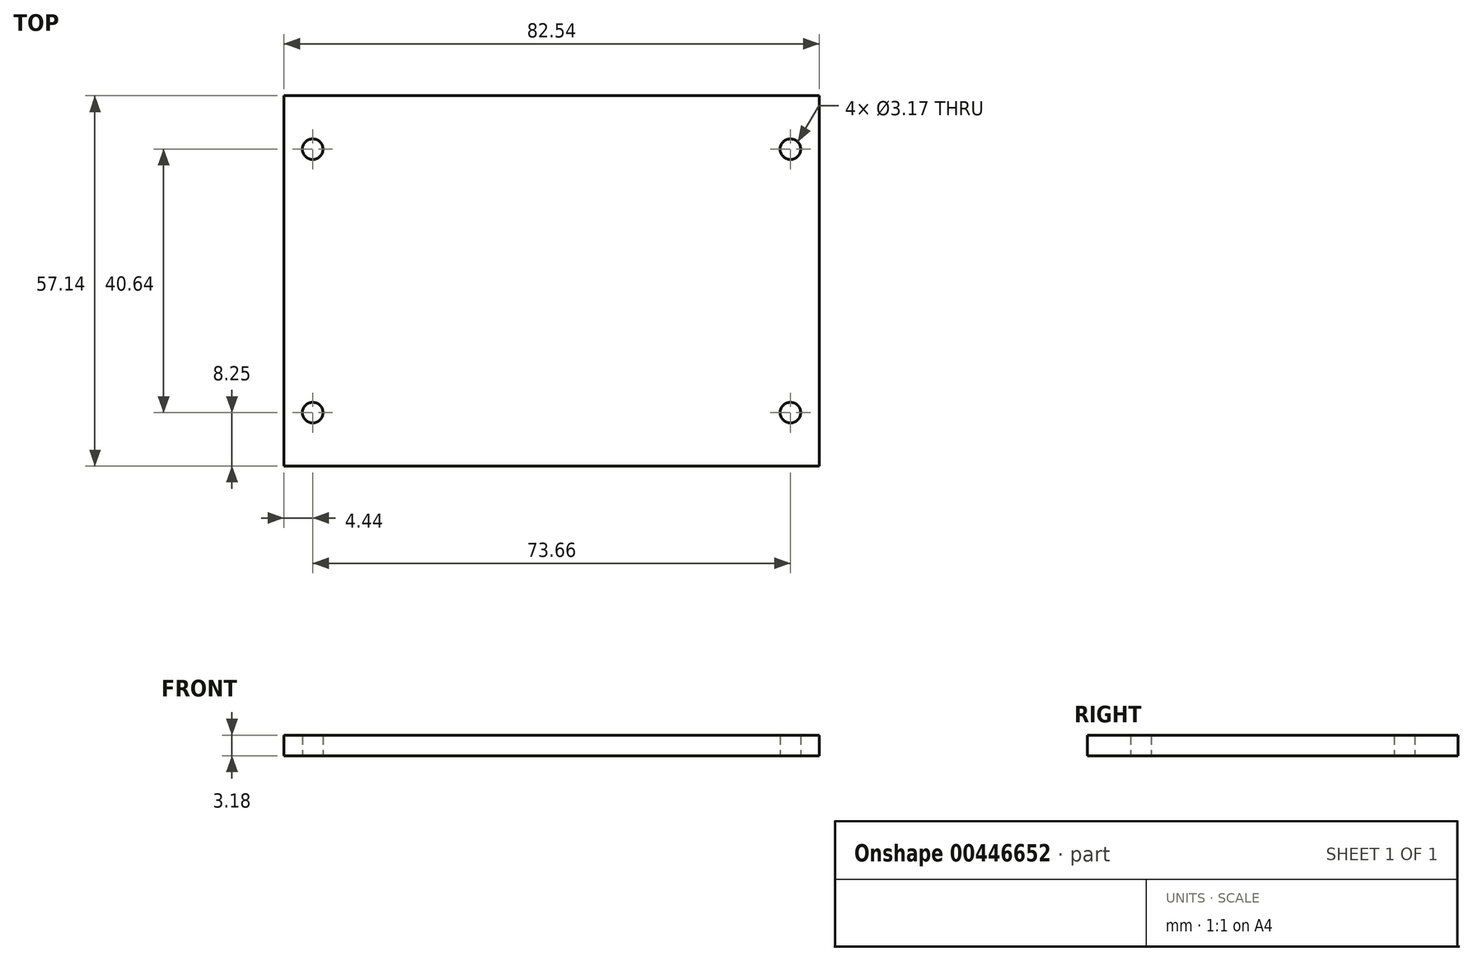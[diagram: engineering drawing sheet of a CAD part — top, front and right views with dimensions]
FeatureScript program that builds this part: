
annotation { "Feature Type Name" : "Feature", "Feature Type Description" : "" }
export const myFeature = defineFeature(function(context is Context, id is Id, definition is map)
    precondition{}
    {
        {
            var Q0;
            Q0=qCreatedBy(makeId("Top.planeOp"),FACE);
            var sketch = newSketch(context, id + "F0", { "sketchPlane" : qUnion([Q0])});
            skLineSegment(sketch, "E0.bottom", {"start": v(36.83, -20.32) * mm, "end": v(-36.83, -20.32) * mm});
            skLineSegment(sketch, "E0.top", {"start": v(36.83, 20.32) * mm, "end": v(-36.83, 20.32) * mm});
            skLineSegment(sketch, "E0.left", {"start": v(36.83, -20.32) * mm, "end": v(36.83, 20.32) * mm});
            skLineSegment(sketch, "E0.right", {"start": v(-36.83, -20.32) * mm, "end": v(-36.83, 20.32) * mm});
            skPoint(sketch, "E0.middle", {"position": v(0, 0) * mm});
            skSolve(sketch);
        }
        {
            var Q0;
            Q0=makeQuery(id+"F0.imprint","IMPRINT",FACE,{"disambiguationData":[TD([[makeQuery(id+"F0.imprint","IMPRINT",EDGE,{"derivedFrom":sQuery(id+"F0.wireOp",EDGE,"E0.bottom")}),-1.0]])]});
            var sketch = newSketch(context, id + "F1", { "sketchPlane" : qUnion([Q0])});
            skLineSegment(sketch, "E1.bottom", {"start": v(41.28, -28.58) * mm, "end": v(-41.28, -28.58) * mm});
            skLineSegment(sketch, "E1.top", {"start": v(41.28, 28.58) * mm, "end": v(-41.28, 28.58) * mm});
            skLineSegment(sketch, "E1.left", {"start": v(41.28, -28.58) * mm, "end": v(41.28, 28.57) * mm});
            skLineSegment(sketch, "E1.right", {"start": v(-41.28, -28.58) * mm, "end": v(-41.28, 28.57) * mm});
            skPoint(sketch, "E1.middle", {"position": v(0, 0) * mm});
            skSolve(sketch);
        }
        {
            var Q0;
            Q0 = qSketchRegion(id + "F1", true);
            extrude(context, id + "F2", {"entities" : qUnion([Q0]), "depth" : 3.17 * mm});
        }
        {
            var Q0;
            Q0=sQuery(id+"F0.wireOp",VERTEX,"E0.bottom.start");
            var Q1;
            Q1=sQuery(id+"F0.wireOp",VERTEX,"E0.left.end");
            var Q2;
            Q2=sQuery(id+"F0.wireOp",VERTEX,"E0.right.end");
            var Q3;
            Q3=sQuery(id+"F0.wireOp",VERTEX,"E0.right.start");
            var Q4;
            Q4=makeQuery(id+"F2.opExtrude","SWEPT_BODY",BODY,{"disambiguationData":[OSD([sQuery(id+"F1.wireOp",EDGE,"E1.bottom"),sQuery(id+"F1.wireOp",EDGE,"E1.top"),sQuery(id+"F1.wireOp",EDGE,"E1.left"),sQuery(id+"F1.wireOp",EDGE,"E1.right")])]});
            hole(context, id + "F3", {"style" : HoleStyle.SIMPLE, "endStyle" : HoleEndStyle.THROUGH, "oppositeDirection" : true, "holeDiameter" : 3.17 * mm, "isTappedThrough" : true, "tappedDepth" : 12.7 * mm, "tapClearance" : 3, "startFromSketch" : true, "locations" : qUnion([Q0, Q1, Q2, Q3]), "scope" : qUnion([Q4])});
        }
    });
